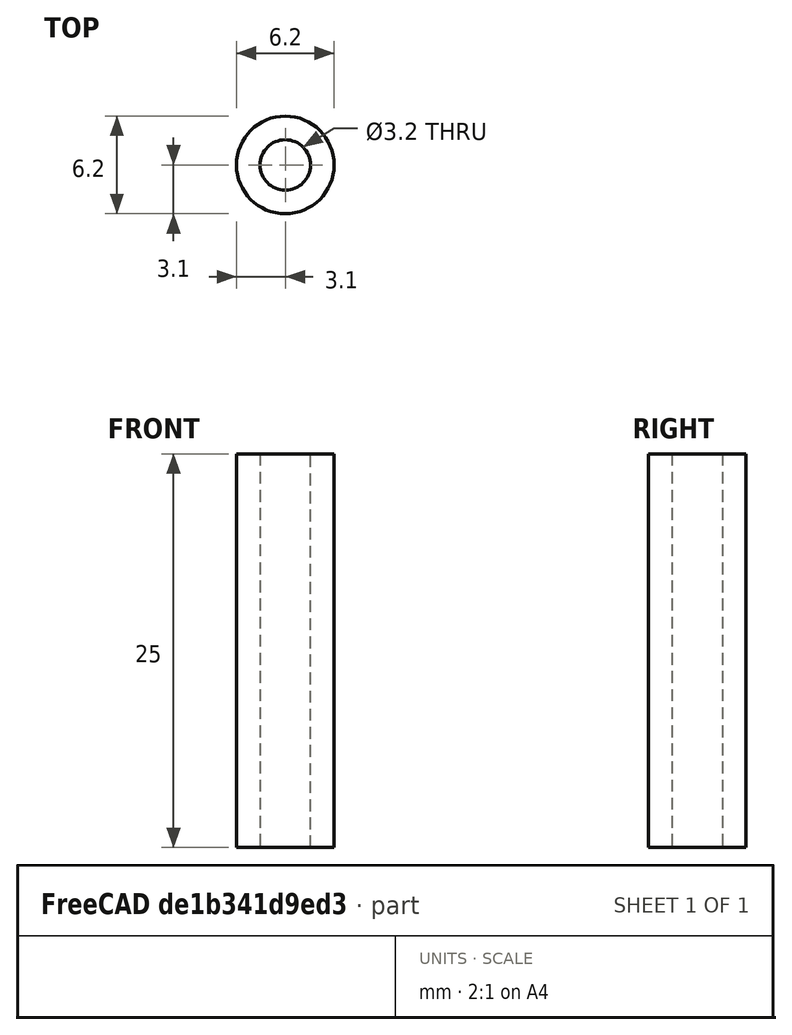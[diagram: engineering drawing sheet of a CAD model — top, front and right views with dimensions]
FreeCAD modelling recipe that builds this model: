
FCSTD DOCUMENT  (FreeCAD 0.20R29603 (Git))
Label: 6D2-3F2-25L
License: All rights reserved
LicenseURL: http://en.wikipedia.org/wiki/All_rights_reserved
objects: Sketcher::SketchObject×1, PartDesign::Pad×1, PartDesign::Body×1
note: 4 computed .brp shape members not serialized (recipe doc carries the construction recipe); baked Part::Feature solids carry a one-line shape summary decoded from their .brp

FEATURE [Sketcher::SketchObject] Sketch
  FullyConstrained = true
  MapMode = 5
  Support = -> [XY_Plane]
  sketch-geometry (4):
    g0: Circle CenterX=0 CenterY=0 CenterZ=0 NormalX=0 NormalY=0 NormalZ=1 AngleXU=0 Radius=3.1
    g1: Circle CenterX=0 CenterY=0 CenterZ=0 NormalX=0 NormalY=0 NormalZ=1 AngleXU=0 Radius=1.6
    g2: GeomPoint X=3.1 Y=0 Z=0
    g3: GeomPoint X=1.6 Y=0 Z=0
  constraints (9):
    c: Coincident(g0,g-1)
    c: Coincident(g1,g0)
    c: Radius(g1) = 1.6
    c: PointOnObject(g3,g1)
    c: PointOnObject(g3,g-1)
    c: PointOnObject(g2,g0)
    c: PointOnObject(g2,g-1)
    c: DistanceX(g3,g2) = 1.5
    c: Radius(g0) = 3.1
FEATURE [PartDesign::Pad] Pad
  Direction = (0,0,1)
  Length = 25
  Length2 = 10
  Profile = -> Sketch
  ReferenceAxis = -> Sketch [N_Axis]
  Type = 0
FEATURE [PartDesign::Body] Body
  Group = -> [Sketch,Pad]
  Origin = -> Origin
  Tip = -> Pad
